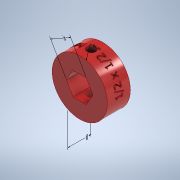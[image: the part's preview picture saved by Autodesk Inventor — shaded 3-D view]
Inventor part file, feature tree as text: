
AUTODESK INVENTOR PART (.ipt)
format: ipt  version: 2022.1 (Build 261234000, 234)  size: 1,108,480 bytes
history: native  units: in
note: dims shown in document units (in); Inventor stores cm internally (conversion verified against a paired STEP export)
features: sketch x5, other x4, extrude x3, plane x2, emboss x1, hole x1
ambient origin geometry x8: Origin, YZ Plane, XZ Plane, XY Plane, X Axis, Y Axis, Z Axis, Center Point
bodies: Solid1 (feature_tree)
feature tree (16):
  other  "Annotations"
  extrude  "Extrusion1"  Depth=1.198in
  plane  "Work Plane1"
  emboss  "Emboss1"
  hole  "Hole1"  [1 undecoded]
  extrude  "Extrusion2"  Depth=0.25in
  plane  "Work Plane2"
  extrude  "Extrusion3"  Depth=0.25in
  sketch  "Sketch1"  dims[d0=0.5in d2=1.198in]
  sketch  "Sketch2"  dims[d3=0.3103in d4=0.5in d5=0.0in]
  sketch  "Sketch3"  dims[d17=1.0in d18=0.25in]
  sketch  "Sketch4"  dims[d19=0.1in d20=0.0in]
  sketch  "Sketch5"  dims[d21=0.17in d22=0.75in d23=0.5in d24=0.093in d25=0.5635in d26=0.25in d27=0.0in d28=0.25in d29=0.25in d30=0.191in d31=0.2186in d32=0.0in d33=0.27in d34=0.073in d35=0.0in d10=0.5245in d11=1.198in d12=0.1538in d13=0.5in d14=0.1112in d15=0.3058in d16=0.5in]
  other  "Diameter Dimension 1"
  other  "Linear Dimension 1"
  other  "Linear Dimension 2"
note: 1 required parameter value undecoded (feature->parameter linkage not recoverable at this tier; creation-order binding heuristic only, values carry confidence <= 0.55)
